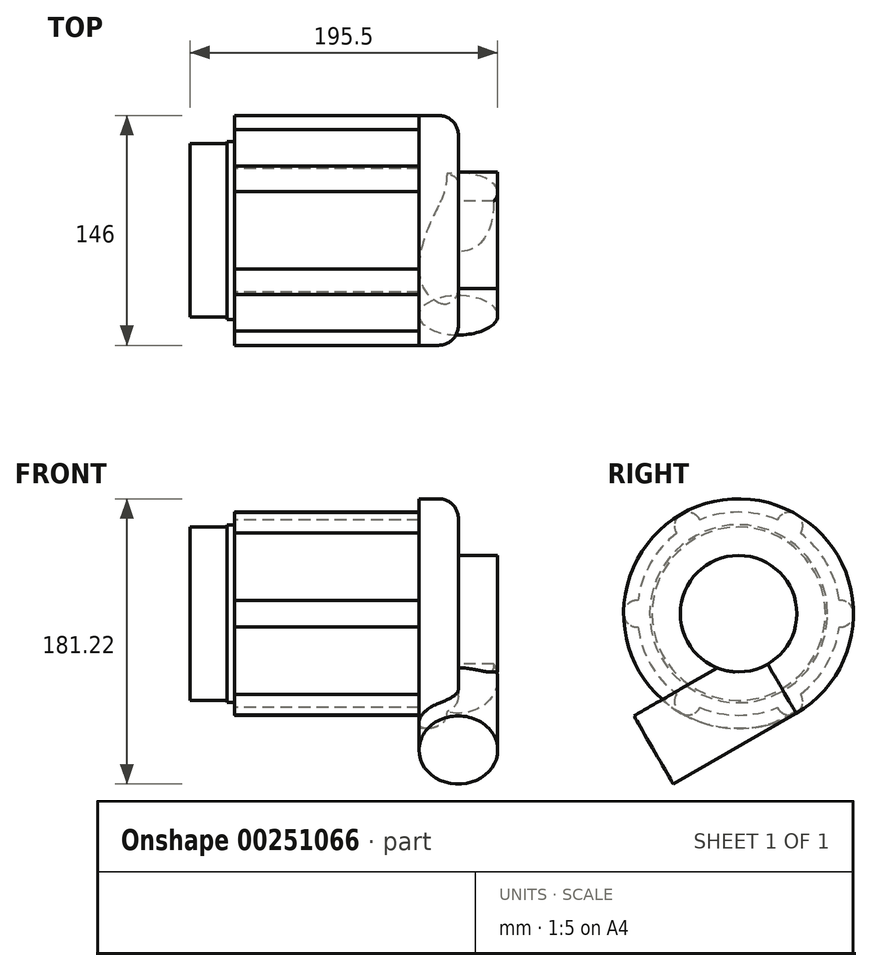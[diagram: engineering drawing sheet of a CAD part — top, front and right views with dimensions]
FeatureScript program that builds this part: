
annotation { "Feature Type Name" : "Feature", "Feature Type Description" : "" }
export const myFeature = defineFeature(function(context is Context, id is Id, definition is map)
    precondition{}
    {
        {
            var Q0;
            Q0=qCreatedBy(makeId("Right.planeOp"),FACE);
            var sketch = newSketch(context, id + "F0", { "sketchPlane" : qUnion([Q0])});
            skCircle(sketch, "E0", {"center": v(0, 0) * mm, "radius": 56.5 * mm});
            skSolve(sketch);
        }
        {
            var Q0;
            Q0 = qSketchRegion(id + "F0", true);
            extrude(context, id + "F1", {"entities" : qUnion([Q0]), "oppositeDirection" : true, "depth" : 5 * mm});
        }
        {
            var Q0;
            Q0=makeQuery(id+"F1.opExtrude","CAP_FACE",FACE,{"disambiguationData":[OSD([sQuery(id+"F0.wireOp",EDGE,"E0")])],"isStart":true});
            var sketch = newSketch(context, id + "F2", { "sketchPlane" : qUnion([Q0])});
            skCircle(sketch, "E1", {"center": v(0, 0) * mm, "radius": 55 * mm});
            skSolve(sketch);
        }
        {
            var Q0;
            Q0 = qSketchRegion(id + "F2", true);
            extrude(context, id + "F3", {"entities" : qUnion([Q0]), "operationType" : NewBodyOperationType.ADD, "oppositeDirection" : true, "depth" : 28.5 * mm});
        }
        {
            var Q0;
            Q0=qCreatedBy(makeId("Right.planeOp"),FACE);
            var sketch = newSketch(context, id + "F4", { "sketchPlane" : qUnion([Q0])});
            skArc(sketch, "E2", {"start": v(24.62, 59.61) * mm, "mid": v(0, 64.5) * mm, "end": v(-24.62, 59.61) * mm});
            skArc(sketch, "E3", {"start": v(-63.94, 8.48) * mm, "mid": v(-73, 0) * mm, "end": v(-63.94, -8.48) * mm});
            skArc(sketch, "E4.1.1", {"start": v(-39.32, -51.13) * mm, "mid": v(-36.5, -63.22) * mm, "end": v(-24.62, -59.61) * mm});
            skArc(sketch, "E4.2.1", {"start": v(24.62, -59.61) * mm, "mid": v(36.5, -63.22) * mm, "end": v(39.32, -51.13) * mm});
            skArc(sketch, "E4.3.1", {"start": v(63.94, -8.48) * mm, "mid": v(73, 0) * mm, "end": v(63.94, 8.48) * mm});
            skArc(sketch, "E4.4.1", {"start": v(39.32, 51.13) * mm, "mid": v(36.5, 63.22) * mm, "end": v(24.62, 59.61) * mm});
            skArc(sketch, "E4.5.1", {"start": v(-24.62, 59.61) * mm, "mid": v(-36.5, 63.22) * mm, "end": v(-39.32, 51.13) * mm});
            skArc(sketch, "E5.trimOffspring", {"start": v(-39.32, 51.13) * mm, "mid": v(-55.86, 32.25) * mm, "end": v(-63.94, 8.48) * mm});
            skArc(sketch, "E6.trimOffspring", {"start": v(-63.94, -8.48) * mm, "mid": v(-55.86, -32.25) * mm, "end": v(-39.32, -51.13) * mm});
            skArc(sketch, "E7.trimOffspring", {"start": v(-24.62, -59.61) * mm, "mid": v(0, -64.5) * mm, "end": v(24.62, -59.61) * mm});
            skArc(sketch, "E8.trimOffspring", {"start": v(39.32, -51.13) * mm, "mid": v(55.86, -32.25) * mm, "end": v(63.94, -8.48) * mm});
            skArc(sketch, "E9.trimOffspring", {"start": v(63.94, 8.48) * mm, "mid": v(55.86, 32.25) * mm, "end": v(39.32, 51.13) * mm});
            skSolve(sketch);
        }
        {
            var Q0;
            Q0 = qSketchRegion(id + "F4", true);
            extrude(context, id + "F5", {"entities" : qUnion([Q0]), "operationType" : NewBodyOperationType.ADD, "depth" : 117 * mm});
        }
        {
            var Q0;
            Q0=qCreatedBy(makeId("Front.planeOp"),FACE);
            var sketch = newSketch(context, id + "F6", { "sketchPlane" : qUnion([Q0])});
            skArc(sketch, "E10", {"start": v(142, 60.5) * mm, "mid": v(138.34, 69.34) * mm, "end": v(129.5, 73) * mm});
            skLineSegment(sketch, "E11", {"start": v(-35.74, 0) * mm, "end": v(197.64, 0) * mm, "construction": true});
            skLineSegment(sketch, "E12", {"start": v(129.5, 73) * mm, "end": v(117, 73) * mm});
            skLineSegment(sketch, "E13", {"start": v(117, 73) * mm, "end": v(117, 0) * mm});
            skLineSegment(sketch, "E14", {"start": v(117, 0) * mm, "end": v(167, 0) * mm});
            skLineSegment(sketch, "E15", {"start": v(167, 0) * mm, "end": v(167, 37) * mm});
            skLineSegment(sketch, "E16", {"start": v(142, 60.5) * mm, "end": v(142, 37) * mm});
            skLineSegment(sketch, "E17", {"start": v(142, 37) * mm, "end": v(167, 37) * mm});
            skPoint(sketch, "E17.endSnap0", {"position": v(167, 18.5) * mm});
            skSolve(sketch);
        }
        {
            var Q0;
            Q0 = qSketchRegion(id + "F6", true);
            var Q1;
            Q1=sQuery(id+"F6.wireOp",EDGE,"E11");
            revolve(context, id + "F7", {"operationType" : NewBodyOperationType.ADD, "entities" : qUnion([Q0]), "axis" : qUnion([Q1]), "revolveType" : RevolveType.FULL});
        }
        {
            var Q0;
            Q0=sQuery(id+"F6.wireOp",EDGE,"E14");
            var Q1;
            Q1=qCreatedBy(makeId("Front.planeOp"),FACE);
            cPlane(context, id + "F8", {"entities" : qUnion([Q0, Q1]), "cplaneType" : CPlaneType.LINE_ANGLE, "offset" : 25 * mm, "angle" : 30 * degree, "width" : 150 * mm, "height" : 150 * mm});
        }
        {
            var Q0;
            Q0=qCreatedBy(id+"F8.planeOp",FACE);
            var sketch = newSketch(context, id + "F9", { "sketchPlane" : qUnion([Q0])});
            skCircle(sketch, "E18", {"center": v(-142, -48) * mm, "radius": 25 * mm});
            skLineSegment(sketch, "E19", {"start": v(-189.52, -73) * mm, "end": v(-73.54, -73) * mm, "construction": true});
            skSolve(sketch);
        }
        {
            var Q0;
            Q0 = qSketchRegion(id + "F9", true);
            extrude(context, id + "F10", {"entities" : qUnion([Q0]), "operationType" : NewBodyOperationType.ADD, "oppositeDirection" : true, "depth" : 90 * mm});
        }
    });
